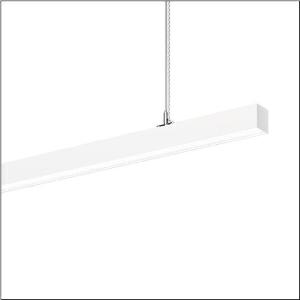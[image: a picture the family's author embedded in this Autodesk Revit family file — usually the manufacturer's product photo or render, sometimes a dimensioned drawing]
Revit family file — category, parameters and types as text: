
# Revit family: silica_21_51mx33db39wb
name_source: partatom
category: Lighting Fixtures
units: mm (PartAtom-declared; Revit-internal decimal feet)

## family parameters
Cut with Voids When Loaded = No
Host = Face
Light Source = No
Part Type = Normal
Room Calculation Point = No
Round Connector Dimension = Use Diameter
Shared = No

## types (1)
- --- (1 x LED, 7390 lm, 51.6 W, 3000K)
    Apparent Load = 52 VA
    CIE Flux Codes = 78 96 99 55 100
    Color Rendering = 80
    Color Temperature = 3000K
    Default Elevation = 1800 mm
    Description = Silica 21, office luminaire, primary optical cover: prismatic diffuser, of PMMA, CAT 2 (L<= 3000cd/m²), light emission: direct/indirect distribution, primary light characteristic: symmetric, installation type: suspended mounting, LED, rated luminous flux: 7.390lm, luminous efficacy: 143lm/W, light colour: 830, colour temperature: 3000K, control gear: DALI 2, with terminal, 3+2-pole, max. 2.5mm², mains connection: 220..240V, AC, 50/60Hz, rated input power: 51.6W, luminaire housing, of aluminium, traffic white (RAL 9016), length: 1.504mm, width: 53mm, height: 53mm, protection rating (complete): IP20, insulation class (complete): insulation class I (protective earthing), certification: CE, permissible operating ambient temperature: 0..+35°C, standard: EN 50419, packaging unit: 1 piece
    Height = 53 mm
    Lamp = 1 x LED
    Lamp Light Flux = 7390 lm
    Lamp Power = 51.6 W
    Lamp count = 1
    Length = 1504 mm
    Luminous efficacy = 143 lm/W
    Manufacturer = Siteco
    ModVariant = No
    Model = 51MX33DB39WB
    Mounting Place = Ceiling
    Mounting Type = Pendant
    Number of Poles = 1
    OnlyDefault = Yes
    Power Factor = 1
    Product Name = Silica 21
    Product group = office luminaire | ceiling pendant
    ProductGroupID = 903
    Protection Class = Protection class I
    Protection Degree = IP 20
    RLX_Detail_Level = 1
    RLX_Emergency_Light_Flux = 0 lm
    RLX_Emergency_Type = 0
    RLX_Emergency_Type_DB = No
    RlxData = <blob elided: 21437 chars, md5=c93ad62a>
    Socket = socket
    Standby Power = 0 W
    System Light Flux = 7390 lm
    System Power = 52 W
    Type Comments = factory setting: luminous flux: 100 % | dim-lin: 254 | 345 mA
    Type Image = l_1349007.jpg
    URL = http://relux.com
    VarID = @adj_119975
    Voltage = 0 V
    Weight = 0.00 kg
    Width = 53 mm

## geometry (parser evidence)
native form markers: Blend x4, Sweep x13
no freeform markers — native parametric forms only
